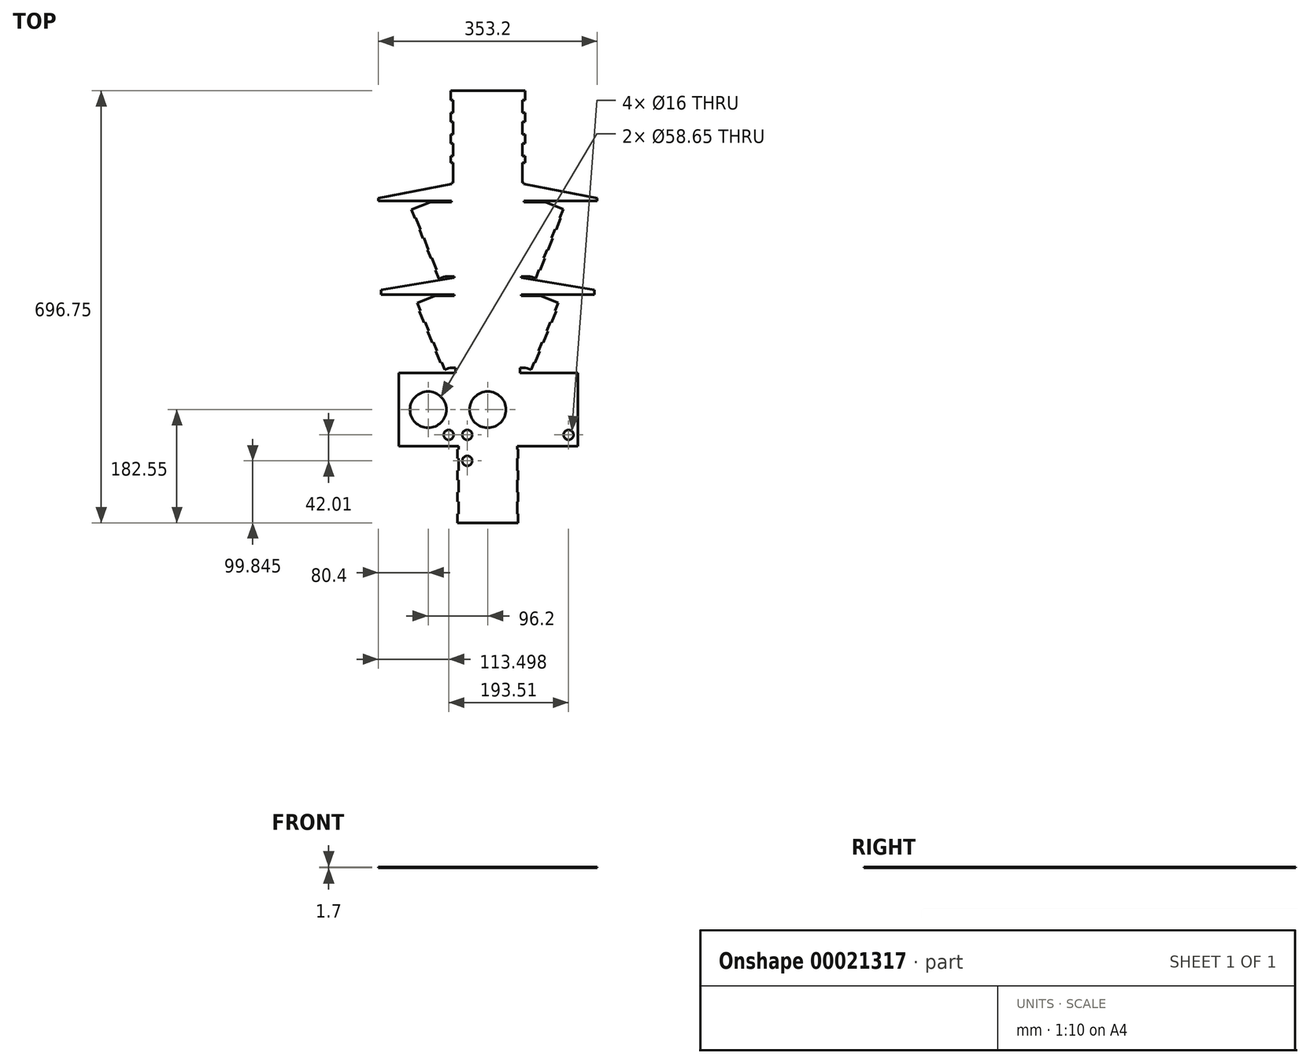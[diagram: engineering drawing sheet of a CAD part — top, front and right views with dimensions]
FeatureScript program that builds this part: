
annotation { "Feature Type Name" : "Feature", "Feature Type Description" : "" }
export const myFeature = defineFeature(function(context is Context, id is Id, definition is map)
    precondition{}
    {
        {
            var Q0;
            Q0=qCreatedBy(makeId("Top.planeOp"),FACE);
            var sketch = newSketch(context, id + "F0", { "sketchPlane" : qUnion([Q0])});
            skCircle(sketch, "E0", {"center": v(0, 0) * mm, "radius": 29.32 * mm, "construction": true});
            skCircle(sketch, "E1", {"center": v(0, 0) * mm, "radius": 34 * mm, "construction": true});
            skLineSegment(sketch, "E2.rect.bottom", {"start": v(60, 60) * mm, "end": v(-60, 60) * mm});
            skLineSegment(sketch, "E2.rect.top", {"start": v(60, -60) * mm, "end": v(-60, -60) * mm});
            skLineSegment(sketch, "E2.rect.left", {"start": v(60, 60) * mm, "end": v(60, -60) * mm});
            skLineSegment(sketch, "E2.rect.right", {"start": v(-60, 60) * mm, "end": v(-60, -60) * mm});
            skLineSegment(sketch, "E3", {"start": v(0, 42.22) * mm, "end": v(0, 43.92) * mm, "construction": true});
            skLineSegment(sketch, "E4", {"start": v(-60, 60) * mm, "end": v(-60, 91) * mm, "construction": true});
            skLineSegment(sketch, "E5", {"start": v(60, -60) * mm, "end": v(68, -60) * mm});
            skLineSegment(sketch, "E6", {"start": v(68, -60) * mm, "end": v(91, 60) * mm});
            skLineSegment(sketch, "E7", {"start": v(91, 60) * mm, "end": v(60, 60) * mm});
            skLineSegment(sketch, "E8", {"start": v(91, 60) * mm, "end": v(92.67, 59.68) * mm});
            skLineSegment(sketch, "E9", {"start": v(69.67, -60.32) * mm, "end": v(68, -60) * mm});
            skLineSegment(sketch, "E10", {"start": v(92.67, 59.68) * mm, "end": v(94.34, 59.36) * mm});
            skLineSegment(sketch, "E11", {"start": v(94.34, 59.36) * mm, "end": v(71.34, -60.64) * mm});
            skLineSegment(sketch, "E12", {"start": v(71.34, -60.64) * mm, "end": v(69.67, -60.32) * mm});
            skLineSegment(sketch, "E13", {"start": v(94.34, 59.36) * mm, "end": v(123.14, 47.9) * mm, "construction": true});
            skLineSegment(sketch, "E14", {"start": v(123.14, 47.9) * mm, "end": v(78.77, -63.6) * mm, "construction": true});
            skLineSegment(sketch, "E15", {"start": v(78.77, -63.6) * mm, "end": v(71.34, -60.64) * mm, "construction": true});
            skLineSegment(sketch, "E16", {"start": v(123.14, 47.9) * mm, "end": v(121.56, 48.53) * mm, "construction": true});
            skLineSegment(sketch, "E17", {"start": v(121.56, 48.53) * mm, "end": v(77.2, -62.97) * mm, "construction": true});
            skLineSegment(sketch, "E18", {"start": v(77.2, -62.97) * mm, "end": v(78.77, -63.6) * mm, "construction": true});
            skLineSegment(sketch, "E19", {"start": v(58.3, 89.3) * mm, "end": v(176.6, 66.3) * mm});
            skLineSegment(sketch, "E20.MirrorCS", {"start": v(-91, 60) * mm, "end": v(-60, 60) * mm});
            skLineSegment(sketch, "E21.MirrorCS", {"start": v(-68, -60) * mm, "end": v(-91, 60) * mm});
            skLineSegment(sketch, "E22.MirrorCS", {"start": v(-94.34, 59.36) * mm, "end": v(-123.14, 47.9) * mm});
            skLineSegment(sketch, "E23.MirrorCS", {"start": v(-94.34, 59.36) * mm, "end": v(-71.34, -60.64) * mm});
            skLineSegment(sketch, "E24.MirrorCS", {"start": v(-121.56, 48.53) * mm, "end": v(-77.2, -62.97) * mm, "construction": true});
            skLineSegment(sketch, "E25.MirrorCS", {"start": v(-123.14, 47.9) * mm, "end": v(-78.77, -63.6) * mm, "construction": true});
            skLineSegment(sketch, "E26.MirrorCS", {"start": v(-91, 60) * mm, "end": v(-92.67, 59.68) * mm});
            skLineSegment(sketch, "E27.MirrorCS", {"start": v(-92.67, 59.68) * mm, "end": v(-94.34, 59.36) * mm});
            skLineSegment(sketch, "E28.MirrorCS", {"start": v(-60, -60) * mm, "end": v(-68, -60) * mm});
            skLineSegment(sketch, "E29.MirrorCS", {"start": v(-69.67, -60.32) * mm, "end": v(-68, -60) * mm});
            skLineSegment(sketch, "E30.MirrorCS", {"start": v(-71.34, -60.64) * mm, "end": v(-69.67, -60.32) * mm});
            skLineSegment(sketch, "E31.MirrorCS", {"start": v(-78.77, -63.6) * mm, "end": v(-71.34, -60.64) * mm, "construction": true});
            skLineSegment(sketch, "E32", {"start": v(123.14, 47.9) * mm, "end": v(117.6, 33.96) * mm, "construction": true});
            skLineSegment(sketch, "E33", {"start": v(117.6, 33.96) * mm, "end": v(116.02, 34.59) * mm});
            skLineSegment(sketch, "E34", {"start": v(116.02, 34.59) * mm, "end": v(108.62, 16) * mm, "construction": true});
            skLineSegment(sketch, "E35", {"start": v(108.62, 16) * mm, "end": v(110.2, 15.38) * mm});
            skLineSegment(sketch, "E36", {"start": v(110.2, 15.38) * mm, "end": v(104.65, 1.44) * mm, "construction": true});
            skLineSegment(sketch, "E37", {"start": v(104.65, 1.44) * mm, "end": v(103.08, 2.07) * mm});
            skLineSegment(sketch, "E38", {"start": v(103.08, 2.07) * mm, "end": v(95.68, -16.51) * mm, "construction": true});
            skLineSegment(sketch, "E39", {"start": v(95.68, -16.51) * mm, "end": v(97.26, -17.14) * mm});
            skLineSegment(sketch, "E40", {"start": v(97.26, -17.14) * mm, "end": v(91.71, -31.08) * mm, "construction": true});
            skLineSegment(sketch, "E41", {"start": v(91.71, -31.08) * mm, "end": v(90.13, -30.45) * mm});
            skLineSegment(sketch, "E42", {"start": v(90.13, -30.45) * mm, "end": v(82.74, -49.03) * mm, "construction": true});
            skLineSegment(sketch, "E43", {"start": v(82.74, -49.03) * mm, "end": v(84.32, -49.66) * mm});
            skLineSegment(sketch, "E44", {"start": v(84.32, -49.66) * mm, "end": v(78.77, -63.6) * mm, "construction": true});
            skLineSegment(sketch, "E45", {"start": v(55.75, 122) * mm, "end": v(55.75, 91) * mm});
            skLineSegment(sketch, "E46", {"start": v(60, 91) * mm, "end": v(-60, 91) * mm, "construction": true});
            skLineSegment(sketch, "E47", {"start": v(-55.75, 92.7) * mm, "end": v(55.75, 92.7) * mm});
            skLineSegment(sketch, "E48", {"start": v(55.75, 122) * mm, "end": v(-55.75, 122) * mm});
            skLineSegment(sketch, "E49", {"start": v(55.75, 122) * mm, "end": v(55.75, 120.3) * mm, "construction": true});
            skLineSegment(sketch, "E50", {"start": v(-55.75, 239.45) * mm, "end": v(-55.75, 122) * mm, "construction": true});
            skLineSegment(sketch, "E51", {"start": v(55.75, 239.45) * mm, "end": v(-55.75, 239.45) * mm});
            skLineSegment(sketch, "E52", {"start": v(55.75, 120.3) * mm, "end": v(55.75, 118.6) * mm, "construction": true});
            skLineSegment(sketch, "E53", {"start": v(55.75, 119.45) * mm, "end": v(55.75, 239.45) * mm, "construction": true});
            skLineSegment(sketch, "E54", {"start": v(56.6, 91) * mm, "end": v(58.3, 91) * mm, "construction": true});
            skLineSegment(sketch, "E55", {"start": v(58.3, 91) * mm, "end": v(60, 91) * mm, "construction": true});
            skLineSegment(sketch, "E56", {"start": v(58.3, 61.7) * mm, "end": v(58.3, 60) * mm});
            skLineSegment(sketch, "E57", {"start": v(58.3, 89.3) * mm, "end": v(58.3, 91) * mm});
            skLineSegment(sketch, "E58", {"start": v(58.3, 89.3) * mm, "end": v(58.3, 61.7) * mm});
            skLineSegment(sketch, "E59", {"start": v(60, 91) * mm, "end": v(60, 60) * mm, "construction": true});
            skLineSegment(sketch, "E60", {"start": v(178.3, 60) * mm, "end": v(178.3, 68) * mm, "construction": true});
            skLineSegment(sketch, "E61", {"start": v(178.3, 61.7) * mm, "end": v(58.3, 61.7) * mm, "construction": true});
            skLineSegment(sketch, "E62", {"start": v(176.6, 66.3) * mm, "end": v(176.6, 61.7) * mm});
            skLineSegment(sketch, "E63", {"start": v(176.6, 61.7) * mm, "end": v(178.3, 61.7) * mm, "construction": true});
            skLineSegment(sketch, "E64", {"start": v(178.3, 61.7) * mm, "end": v(178.3, 60) * mm, "construction": true});
            skLineSegment(sketch, "E65", {"start": v(178.3, 68) * mm, "end": v(178.3, 66.3) * mm, "construction": true});
            skLineSegment(sketch, "E66.MirrorCS", {"start": v(-58.3, 89.3) * mm, "end": v(-176.6, 66.3) * mm});
            skLineSegment(sketch, "E67.MirrorCS", {"start": v(-176.6, 66.3) * mm, "end": v(-176.6, 61.7) * mm});
            skLineSegment(sketch, "E68.MirrorCS", {"start": v(-58.3, 89.3) * mm, "end": v(-58.3, 91) * mm});
            skLineSegment(sketch, "E69.MirrorCS", {"start": v(-58.3, 89.3) * mm, "end": v(-58.3, 61.7) * mm});
            skLineSegment(sketch, "E70.MirrorCS", {"start": v(-58.3, 61.7) * mm, "end": v(-58.3, 60) * mm});
            skLineSegment(sketch, "E71", {"start": v(176.6, 61.7) * mm, "end": v(58.3, 61.7) * mm});
            skLineSegment(sketch, "E72.MirrorCS", {"start": v(-176.6, 61.7) * mm, "end": v(-58.3, 61.7) * mm});
            skLineSegment(sketch, "E73", {"start": v(55.75, 92.7) * mm, "end": v(55.75, 91) * mm, "construction": true});
            skLineSegment(sketch, "E74", {"start": v(55.75, 239.45) * mm, "end": v(60, 239.45) * mm});
            skLineSegment(sketch, "E75", {"start": v(60, 239.45) * mm, "end": v(60, 224.45) * mm});
            skLineSegment(sketch, "E76", {"start": v(60, 224.45) * mm, "end": v(55.75, 224.45) * mm});
            skLineSegment(sketch, "E77", {"start": v(55.75, 224.45) * mm, "end": v(55.75, 204.45) * mm});
            skLineSegment(sketch, "E78", {"start": v(55.75, 204.45) * mm, "end": v(60, 204.45) * mm});
            skLineSegment(sketch, "E79", {"start": v(60, 204.45) * mm, "end": v(60, 189.45) * mm});
            skLineSegment(sketch, "E80", {"start": v(60, 189.45) * mm, "end": v(55.75, 189.45) * mm});
            skLineSegment(sketch, "E81", {"start": v(55.75, 189.45) * mm, "end": v(55.75, 169.45) * mm});
            skLineSegment(sketch, "E82", {"start": v(55.75, 169.45) * mm, "end": v(60, 169.45) * mm});
            skLineSegment(sketch, "E83", {"start": v(60, 169.45) * mm, "end": v(60, 154.45) * mm});
            skLineSegment(sketch, "E84", {"start": v(60, 154.45) * mm, "end": v(55.75, 154.45) * mm});
            skLineSegment(sketch, "E85", {"start": v(55.75, 154.45) * mm, "end": v(55.75, 134.45) * mm});
            skLineSegment(sketch, "E86", {"start": v(55.75, 134.45) * mm, "end": v(60, 134.45) * mm});
            skLineSegment(sketch, "E87", {"start": v(60, 134.45) * mm, "end": v(60, 123.7) * mm});
            skLineSegment(sketch, "E88", {"start": v(55.75, 123.7) * mm, "end": v(55.75, 122) * mm, "construction": true});
            skLineSegment(sketch, "E89", {"start": v(55.75, 123.7) * mm, "end": v(55.75, 122) * mm});
            skLineSegment(sketch, "E90", {"start": v(60, 123.7) * mm, "end": v(55.75, 123.7) * mm});
            skLineSegment(sketch, "E91", {"start": v(55.75, -91) * mm, "end": v(-55.75, -91) * mm});
            skLineSegment(sketch, "E92", {"start": v(-55.75, -91) * mm, "end": v(-55.75, -60) * mm, "construction": true});
            skLineSegment(sketch, "E93", {"start": v(55.75, -91) * mm, "end": v(55.75, -60) * mm, "construction": true});
            skLineSegment(sketch, "E94", {"start": v(55.75, -60) * mm, "end": v(54.05, -60) * mm});
            skLineSegment(sketch, "E95", {"start": v(54.05, -60) * mm, "end": v(54.05, -61.7) * mm});
            skLineSegment(sketch, "E96", {"start": v(54.05, -61.7) * mm, "end": v(172.35, -81.3) * mm});
            skLineSegment(sketch, "E97", {"start": v(54.05, -91) * mm, "end": v(54.05, -89.3) * mm});
            skLineSegment(sketch, "E98", {"start": v(54.05, -89.3) * mm, "end": v(172.35, -89.3) * mm});
            skLineSegment(sketch, "E99", {"start": v(172.35, -89.3) * mm, "end": v(172.35, -81.3) * mm});
            skLineSegment(sketch, "E100", {"start": v(57.45, 91) * mm, "end": v(55.75, 91) * mm});
            skLineSegment(sketch, "E101", {"start": v(-60, -60) * mm, "end": v(-55.75, -60) * mm});
            skLineSegment(sketch, "E102", {"start": v(55.75, -60) * mm, "end": v(60, -60) * mm});
            skLineSegment(sketch, "E103.MirrorCS", {"start": v(-172.35, -89.3) * mm, "end": v(-172.35, -81.3) * mm});
            skLineSegment(sketch, "E104.MirrorCS", {"start": v(-54.05, -61.7) * mm, "end": v(-172.35, -81.3) * mm});
            skLineSegment(sketch, "E105.MirrorCS", {"start": v(-54.05, -89.3) * mm, "end": v(-172.35, -89.3) * mm});
            skLineSegment(sketch, "E106.MirrorCS", {"start": v(-54.05, -60) * mm, "end": v(-54.05, -61.7) * mm});
            skLineSegment(sketch, "E107.MirrorCS", {"start": v(-55.75, -60) * mm, "end": v(-54.05, -60) * mm});
            skLineSegment(sketch, "E108.MirrorCS", {"start": v(-54.05, -91) * mm, "end": v(-54.05, -89.3) * mm, "construction": true});
            skLineSegment(sketch, "E109", {"start": v(54.05, -91) * mm, "end": v(52.35, -91) * mm, "construction": true});
            skLineSegment(sketch, "E110", {"start": v(-54.05, -91) * mm, "end": v(-52.35, -91) * mm, "construction": true});
            skLineSegment(sketch, "E111", {"start": v(52.35, -91) * mm, "end": v(52.35, -211) * mm});
            skLineSegment(sketch, "E112", {"start": v(52.35, -211) * mm, "end": v(52.35, -209.3) * mm, "construction": true});
            skLineSegment(sketch, "E113", {"start": v(52.35, -209.3) * mm, "end": v(52.35, -207.6) * mm, "construction": true});
            skLineSegment(sketch, "E114", {"start": v(52.35, -207.6) * mm, "end": v(-52.35, -207.6) * mm});
            skLineSegment(sketch, "E115", {"start": v(-52.35, -207.6) * mm, "end": v(-52.35, -91) * mm});
            skLineSegment(sketch, "E116", {"start": v(52.35, -207.6) * mm, "end": v(60.35, -207.6) * mm});
            skLineSegment(sketch, "E117", {"start": v(60.35, -207.6) * mm, "end": v(83.35, -91) * mm});
            skLineSegment(sketch, "E118", {"start": v(83.35, -91) * mm, "end": v(52.35, -91) * mm, "construction": true});
            skLineSegment(sketch, "E119", {"start": v(83.35, -91) * mm, "end": v(86.69, -91.66) * mm});
            skLineSegment(sketch, "E120", {"start": v(86.69, -91.66) * mm, "end": v(63.69, -208.26) * mm});
            skLineSegment(sketch, "E121", {"start": v(60.35, -207.6) * mm, "end": v(62.02, -207.93) * mm});
            skLineSegment(sketch, "E122", {"start": v(62.02, -207.93) * mm, "end": v(63.69, -208.26) * mm});
            skLineSegment(sketch, "E123", {"start": v(86.69, -91.66) * mm, "end": v(115.36, -103.43) * mm, "construction": true});
            skLineSegment(sketch, "E124", {"start": v(115.36, -103.43) * mm, "end": v(71.09, -211.3) * mm, "construction": true});
            skLineSegment(sketch, "E125", {"start": v(71.09, -211.3) * mm, "end": v(63.69, -208.26) * mm, "construction": true});
            skLineSegment(sketch, "E126", {"start": v(-52.35, -207.6) * mm, "end": v(-60.35, -207.6) * mm});
            skLineSegment(sketch, "E127", {"start": v(-60.35, -207.6) * mm, "end": v(-83.35, -91) * mm});
            skLineSegment(sketch, "E128", {"start": v(-83.35, -91) * mm, "end": v(-52.35, -91) * mm, "construction": true});
            skLineSegment(sketch, "E129", {"start": v(-83.35, -91) * mm, "end": v(-86.69, -91.66) * mm});
            skLineSegment(sketch, "E130", {"start": v(-86.69, -91.66) * mm, "end": v(-63.69, -208.26) * mm});
            skLineSegment(sketch, "E131", {"start": v(-63.69, -208.26) * mm, "end": v(-60.35, -207.6) * mm});
            skLineSegment(sketch, "E132", {"start": v(-86.69, -91.66) * mm, "end": v(-115.36, -103.43) * mm, "construction": true});
            skLineSegment(sketch, "E133", {"start": v(-115.36, -103.43) * mm, "end": v(-71.09, -211.3) * mm, "construction": true});
            skLineSegment(sketch, "E134", {"start": v(-71.09, -211.3) * mm, "end": v(-63.69, -208.26) * mm, "construction": true});
            skLineSegment(sketch, "E135", {"start": v(-47.25, -215.6) * mm, "end": v(47.25, -215.6) * mm});
            skLineSegment(sketch, "E136", {"start": v(47.25, -215.6) * mm, "end": v(47.25, -332.2) * mm});
            skLineSegment(sketch, "E137", {"start": v(-47.25, -333.9) * mm, "end": v(-47.25, -215.6) * mm});
            skLineSegment(sketch, "E138", {"start": v(47.25, -333.9) * mm, "end": v(47.25, -332.2) * mm, "construction": true});
            skLineSegment(sketch, "E139", {"start": v(47.25, -333.9) * mm, "end": v(-47.25, -333.9) * mm});
            skLineSegment(sketch, "E140", {"start": v(50.65, -215.6) * mm, "end": v(50.65, -333.9) * mm});
            skLineSegment(sketch, "E141", {"start": v(50.65, -333.9) * mm, "end": v(47.25, -333.9) * mm});
            skLineSegment(sketch, "E142", {"start": v(47.25, -215.6) * mm, "end": v(48.95, -215.6) * mm, "construction": true});
            skLineSegment(sketch, "E143", {"start": v(48.95, -215.6) * mm, "end": v(50.65, -215.6) * mm, "construction": true});
            skLineSegment(sketch, "E144", {"start": v(-47.25, -215.6) * mm, "end": v(-48.95, -215.6) * mm, "construction": true});
            skLineSegment(sketch, "E145", {"start": v(-48.95, -215.6) * mm, "end": v(-48.95, -333.9) * mm});
            skLineSegment(sketch, "E146", {"start": v(-48.95, -333.9) * mm, "end": v(-47.25, -333.9) * mm});
            skLineSegment(sketch, "E147", {"start": v(0, -215.6) * mm, "end": v(0, -274.75) * mm, "construction": true});
            skLineSegment(sketch, "E148", {"start": v(0, -274.75) * mm, "end": v(-47.25, -274.75) * mm, "construction": true});
            skCircle(sketch, "E149", {"center": v(0, -274.75) * mm, "radius": 29.32 * mm});
            skLineSegment(sketch, "E150", {"start": v(52.35, -207.6) * mm, "end": v(50.65, -207.6) * mm, "construction": true});
            skLineSegment(sketch, "E151", {"start": v(50.65, -207.6) * mm, "end": v(48.95, -207.6) * mm, "construction": true});
            skLineSegment(sketch, "E152", {"start": v(48.95, -207.6) * mm, "end": v(47.25, -207.6) * mm, "construction": true});
            skLineSegment(sketch, "E153", {"start": v(47.25, -215.6) * mm, "end": v(-47.25, -215.6) * mm});
            skPoint(sketch, "E154", {"position": v(0, -207.6) * mm});
            skPoint(sketch, "E155", {"position": v(0, -215.6) * mm});
            skLineSegment(sketch, "E156", {"start": v(-47.25, -207.6) * mm, "end": v(-52.35, -207.6) * mm, "construction": true});
            skLineSegment(sketch, "E157", {"start": v(-52.35, -207.6) * mm, "end": v(-52.35, -215.6) * mm});
            skLineSegment(sketch, "E158", {"start": v(-52.35, -215.6) * mm, "end": v(-47.25, -215.6) * mm, "construction": true});
            skLineSegment(sketch, "E159", {"start": v(52.35, -207.6) * mm, "end": v(52.35, -215.6) * mm});
            skLineSegment(sketch, "E160", {"start": v(52.35, -215.6) * mm, "end": v(47.25, -215.6) * mm, "construction": true});
            skLineSegment(sketch, "E161", {"start": v(-48.95, -333.9) * mm, "end": v(-143.45, -333.9) * mm});
            skLineSegment(sketch, "E162", {"start": v(-143.45, -333.9) * mm, "end": v(-143.45, -215.6) * mm});
            skLineSegment(sketch, "E163", {"start": v(-143.45, -215.6) * mm, "end": v(-48.95, -215.6) * mm, "construction": true});
            skLineSegment(sketch, "E164", {"start": v(50.65, -215.6) * mm, "end": v(145.15, -215.6) * mm, "construction": true});
            skLineSegment(sketch, "E165", {"start": v(145.15, -215.6) * mm, "end": v(145.15, -333.9) * mm});
            skLineSegment(sketch, "E166", {"start": v(145.15, -333.9) * mm, "end": v(50.65, -333.9) * mm});
            skLineSegment(sketch, "E167", {"start": v(-47.25, -333.9) * mm, "end": v(-47.25, -339) * mm});
            skLineSegment(sketch, "E168", {"start": v(-47.25, -339) * mm, "end": v(47.25, -339) * mm});
            skLineSegment(sketch, "E169", {"start": v(47.25, -333.9) * mm, "end": v(47.25, -335.6) * mm});
            skLineSegment(sketch, "E170", {"start": v(47.25, -335.6) * mm, "end": v(47.25, -339) * mm});
            skLineSegment(sketch, "E171", {"start": v(-47.25, -339) * mm, "end": v(-47.25, -457.3) * mm, "construction": true});
            skLineSegment(sketch, "E172", {"start": v(-47.25, -457.3) * mm, "end": v(47.25, -457.3) * mm});
            skLineSegment(sketch, "E173", {"start": v(47.25, -457.3) * mm, "end": v(47.25, -339) * mm, "construction": true});
            skLineSegment(sketch, "E174", {"start": v(-96.2, -215.6) * mm, "end": v(-96.2, -274.75) * mm, "construction": true});
            skLineSegment(sketch, "E175", {"start": v(-96.2, -274.75) * mm, "end": v(-48.95, -274.75) * mm, "construction": true});
            skCircle(sketch, "E176", {"center": v(-96.2, -274.75) * mm, "radius": 29.32 * mm});
            skLineSegment(sketch, "E177", {"start": v(47.25, -457.3) * mm, "end": v(48.95, -457.3) * mm});
            skLineSegment(sketch, "E178", {"start": v(48.95, -339) * mm, "end": v(47.25, -339) * mm});
            skLineSegment(sketch, "E179", {"start": v(-47.25, -339) * mm, "end": v(-48.95, -339) * mm});
            skLineSegment(sketch, "E180", {"start": v(-48.95, -457.3) * mm, "end": v(-47.25, -457.3) * mm});
            skLineSegment(sketch, "E181", {"start": v(48.95, -339) * mm, "end": v(48.95, -353.15) * mm});
            skLineSegment(sketch, "E182", {"start": v(48.95, -353.15) * mm, "end": v(47.25, -353.15) * mm});
            skLineSegment(sketch, "E183", {"start": v(47.25, -353.15) * mm, "end": v(47.25, -373.15) * mm});
            skLineSegment(sketch, "E184", {"start": v(47.25, -373.15) * mm, "end": v(48.95, -373.15) * mm});
            skLineSegment(sketch, "E185", {"start": v(48.95, -373.15) * mm, "end": v(48.95, -388.15) * mm});
            skLineSegment(sketch, "E186", {"start": v(48.95, -388.15) * mm, "end": v(47.25, -388.15) * mm});
            skLineSegment(sketch, "E187", {"start": v(47.25, -408.15) * mm, "end": v(47.25, -388.15) * mm});
            skLineSegment(sketch, "E188", {"start": v(47.25, -408.15) * mm, "end": v(48.95, -408.15) * mm});
            skLineSegment(sketch, "E189", {"start": v(48.95, -408.15) * mm, "end": v(48.95, -423.15) * mm});
            skLineSegment(sketch, "E190", {"start": v(48.95, -423.15) * mm, "end": v(47.25, -423.15) * mm});
            skLineSegment(sketch, "E191", {"start": v(47.25, -423.15) * mm, "end": v(47.25, -443.15) * mm});
            skLineSegment(sketch, "E192", {"start": v(47.25, -443.15) * mm, "end": v(48.95, -443.15) * mm});
            skLineSegment(sketch, "E193", {"start": v(48.95, -443.15) * mm, "end": v(48.95, -457.3) * mm});
            skLineSegment(sketch, "E194.MirrorCS", {"start": v(-48.95, -443.15) * mm, "end": v(-48.95, -457.3) * mm});
            skLineSegment(sketch, "E195.MirrorCS", {"start": v(-48.95, -408.15) * mm, "end": v(-48.95, -423.15) * mm});
            skLineSegment(sketch, "E196.MirrorCS", {"start": v(-48.95, -373.15) * mm, "end": v(-48.95, -388.15) * mm});
            skLineSegment(sketch, "E197.MirrorCS", {"start": v(-48.95, -339) * mm, "end": v(-48.95, -353.15) * mm});
            skLineSegment(sketch, "E198.MirrorCS", {"start": v(-48.95, -339) * mm, "end": v(-47.25, -339) * mm});
            skLineSegment(sketch, "E199.MirrorCS", {"start": v(-48.95, -353.15) * mm, "end": v(-47.25, -353.15) * mm});
            skLineSegment(sketch, "E200.MirrorCS", {"start": v(-47.25, -373.15) * mm, "end": v(-48.95, -373.15) * mm});
            skLineSegment(sketch, "E201.MirrorCS", {"start": v(-48.95, -388.15) * mm, "end": v(-47.25, -388.15) * mm});
            skLineSegment(sketch, "E202.MirrorCS", {"start": v(-47.25, -408.15) * mm, "end": v(-48.95, -408.15) * mm});
            skLineSegment(sketch, "E203.MirrorCS", {"start": v(-48.95, -423.15) * mm, "end": v(-47.25, -423.15) * mm});
            skLineSegment(sketch, "E204.MirrorCS", {"start": v(-47.25, -457.3) * mm, "end": v(-48.95, -457.3) * mm});
            skLineSegment(sketch, "E205.MirrorCS", {"start": v(-47.25, -443.15) * mm, "end": v(-48.95, -443.15) * mm});
            skLineSegment(sketch, "E206.MirrorCS", {"start": v(-47.25, -423.15) * mm, "end": v(-47.25, -443.15) * mm});
            skLineSegment(sketch, "E207.MirrorCS", {"start": v(-47.25, -353.15) * mm, "end": v(-47.25, -373.15) * mm});
            skLineSegment(sketch, "E208.MirrorCS", {"start": v(-47.25, -408.15) * mm, "end": v(-47.25, -388.15) * mm});
            skLineSegment(sketch, "E209.MirrorCS", {"start": v(-82.74, -49.03) * mm, "end": v(-84.32, -49.66) * mm});
            skLineSegment(sketch, "E210.MirrorCS", {"start": v(-77.2, -62.97) * mm, "end": v(-78.77, -63.6) * mm});
            skLineSegment(sketch, "E211.MirrorCS", {"start": v(-84.32, -49.66) * mm, "end": v(-78.77, -63.6) * mm});
            skLineSegment(sketch, "E212.MirrorCS", {"start": v(-90.13, -30.45) * mm, "end": v(-82.74, -49.03) * mm});
            skLineSegment(sketch, "E213.MirrorCS", {"start": v(-91.71, -31.08) * mm, "end": v(-90.13, -30.45) * mm});
            skLineSegment(sketch, "E214.MirrorCS", {"start": v(-97.26, -17.14) * mm, "end": v(-91.71, -31.08) * mm});
            skLineSegment(sketch, "E215.MirrorCS", {"start": v(-95.68, -16.51) * mm, "end": v(-97.26, -17.14) * mm});
            skLineSegment(sketch, "E216.MirrorCS", {"start": v(-104.65, 1.44) * mm, "end": v(-103.08, 2.07) * mm});
            skLineSegment(sketch, "E217.MirrorCS", {"start": v(-103.08, 2.07) * mm, "end": v(-95.68, -16.51) * mm});
            skLineSegment(sketch, "E218.MirrorCS", {"start": v(-108.62, 16) * mm, "end": v(-110.2, 15.38) * mm});
            skLineSegment(sketch, "E219.MirrorCS", {"start": v(-110.2, 15.38) * mm, "end": v(-104.65, 1.44) * mm});
            skLineSegment(sketch, "E220.MirrorCS", {"start": v(-117.6, 33.96) * mm, "end": v(-116.02, 34.59) * mm});
            skLineSegment(sketch, "E221.MirrorCS", {"start": v(-116.02, 34.59) * mm, "end": v(-108.62, 16) * mm});
            skLineSegment(sketch, "E222.MirrorCS", {"start": v(-123.14, 47.9) * mm, "end": v(-121.56, 48.53) * mm});
            skLineSegment(sketch, "E223.MirrorCS", {"start": v(-123.14, 47.9) * mm, "end": v(-117.6, 33.96) * mm});
            skLineSegment(sketch, "E224.MirrorCS", {"start": v(-60, 204.45) * mm, "end": v(-60, 189.45) * mm});
            skLineSegment(sketch, "E225.MirrorCS", {"start": v(-60, 189.45) * mm, "end": v(-55.75, 189.45) * mm});
            skLineSegment(sketch, "E226.MirrorCS", {"start": v(-55.75, 189.45) * mm, "end": v(-55.75, 169.45) * mm});
            skLineSegment(sketch, "E227.MirrorCS", {"start": v(-55.75, 204.45) * mm, "end": v(-60, 204.45) * mm});
            skLineSegment(sketch, "E228.MirrorCS", {"start": v(-55.75, 169.45) * mm, "end": v(-60, 169.45) * mm});
            skLineSegment(sketch, "E229.MirrorCS", {"start": v(-60, 169.45) * mm, "end": v(-60, 154.45) * mm});
            skLineSegment(sketch, "E230.MirrorCS", {"start": v(-60, 154.45) * mm, "end": v(-55.75, 154.45) * mm});
            skLineSegment(sketch, "E231.MirrorCS", {"start": v(-55.75, 154.45) * mm, "end": v(-55.75, 134.45) * mm});
            skLineSegment(sketch, "E232.MirrorCS", {"start": v(-55.75, 134.45) * mm, "end": v(-60, 134.45) * mm});
            skLineSegment(sketch, "E233.MirrorCS", {"start": v(-55.75, 224.45) * mm, "end": v(-55.75, 204.45) * mm});
            skLineSegment(sketch, "E234.MirrorCS", {"start": v(-55.75, 239.45) * mm, "end": v(-60, 239.45) * mm});
            skLineSegment(sketch, "E235.MirrorCS", {"start": v(-60, 239.45) * mm, "end": v(-60, 224.45) * mm});
            skLineSegment(sketch, "E236.MirrorCS", {"start": v(-60, 224.45) * mm, "end": v(-55.75, 224.45) * mm});
            skLineSegment(sketch, "E237.MirrorCS", {"start": v(-60, 134.45) * mm, "end": v(-60, 123.7) * mm});
            skLineSegment(sketch, "E238.MirrorCS", {"start": v(-60, 123.7) * mm, "end": v(-55.75, 123.7) * mm});
            skPoint(sketch, "E239", {"position": v(0, 92.7) * mm});
            skPoint(sketch, "E240", {"position": v(0, 60) * mm});
            skLineSegment(sketch, "E241", {"start": v(-55.75, 92.7) * mm, "end": v(-55.75, 91) * mm});
            skLineSegment(sketch, "E242", {"start": v(-55.75, 122) * mm, "end": v(-55.75, 92.7) * mm});
            skLineSegment(sketch, "E243", {"start": v(-55.75, 123.7) * mm, "end": v(-55.75, 122) * mm});
            skLineSegment(sketch, "E244", {"start": v(-58.3, 91) * mm, "end": v(-55.75, 91) * mm});
            skLineSegment(sketch, "E245", {"start": v(-58.3, 60) * mm, "end": v(-60, 60) * mm});
            skLineSegment(sketch, "E246", {"start": v(-77.2, -62.97) * mm, "end": v(-71.34, -60.64) * mm});
            skLineSegment(sketch, "E247", {"start": v(-52.35, -91) * mm, "end": v(-54.05, -91) * mm, "construction": true});
            skLineSegment(sketch, "E248", {"start": v(-55.75, -91) * mm, "end": v(-83.35, -91) * mm});
            skLineSegment(sketch, "E249", {"start": v(58.3, 60) * mm, "end": v(60, 60) * mm});
            skLineSegment(sketch, "E250", {"start": v(94.34, 59.36) * mm, "end": v(121.56, 48.53) * mm});
            skLineSegment(sketch, "E251", {"start": v(121.56, 48.53) * mm, "end": v(116.02, 34.59) * mm});
            skLineSegment(sketch, "E252", {"start": v(117.6, 33.96) * mm, "end": v(110.2, 15.38) * mm});
            skLineSegment(sketch, "E253", {"start": v(108.62, 16) * mm, "end": v(103.08, 2.07) * mm});
            skLineSegment(sketch, "E254", {"start": v(104.65, 1.44) * mm, "end": v(97.26, -17.14) * mm});
            skLineSegment(sketch, "E255", {"start": v(95.68, -16.51) * mm, "end": v(90.13, -30.45) * mm});
            skLineSegment(sketch, "E256", {"start": v(91.71, -31.08) * mm, "end": v(84.32, -49.66) * mm});
            skLineSegment(sketch, "E257", {"start": v(82.74, -49.03) * mm, "end": v(77.2, -62.97) * mm});
            skLineSegment(sketch, "E258", {"start": v(77.2, -62.97) * mm, "end": v(71.34, -60.64) * mm});
            skLineSegment(sketch, "E259", {"start": v(-71.09, -211.3) * mm, "end": v(-69.51, -210.65) * mm, "construction": true});
            skLineSegment(sketch, "E260", {"start": v(-69.51, -210.65) * mm, "end": v(-74.56, -198.35) * mm});
            skLineSegment(sketch, "E261", {"start": v(-74.56, -198.35) * mm, "end": v(-76.14, -199) * mm});
            skLineSegment(sketch, "E262", {"start": v(-76.14, -199) * mm, "end": v(-83.73, -180.5) * mm});
            skLineSegment(sketch, "E263", {"start": v(-83.73, -180.5) * mm, "end": v(-82.16, -179.84) * mm});
            skLineSegment(sketch, "E264", {"start": v(-82.16, -179.84) * mm, "end": v(-87.86, -165.97) * mm});
            skLineSegment(sketch, "E265", {"start": v(-87.86, -165.97) * mm, "end": v(-89.43, -166.61) * mm});
            skLineSegment(sketch, "E266", {"start": v(-89.43, -166.61) * mm, "end": v(-97.02, -148.11) * mm});
            skLineSegment(sketch, "E267", {"start": v(-97.02, -148.11) * mm, "end": v(-95.45, -147.47) * mm});
            skLineSegment(sketch, "E268", {"start": v(-95.45, -147.47) * mm, "end": v(-101.15, -133.59) * mm});
            skLineSegment(sketch, "E269", {"start": v(-101.15, -133.59) * mm, "end": v(-102.72, -134.24) * mm});
            skLineSegment(sketch, "E270", {"start": v(-102.72, -134.24) * mm, "end": v(-110.31, -115.73) * mm});
            skLineSegment(sketch, "E271", {"start": v(-110.31, -115.73) * mm, "end": v(-108.74, -115.09) * mm});
            skLineSegment(sketch, "E272", {"start": v(-108.74, -115.09) * mm, "end": v(-113.8, -102.78) * mm});
            skLineSegment(sketch, "E273", {"start": v(-113.8, -102.78) * mm, "end": v(-115.36, -103.43) * mm, "construction": true});
            skLineSegment(sketch, "E274", {"start": v(-63.69, -208.26) * mm, "end": v(-69.51, -210.65) * mm});
            skLineSegment(sketch, "E275", {"start": v(-113.8, -102.78) * mm, "end": v(-86.69, -91.66) * mm});
            skLineSegment(sketch, "E276.MirrorCS", {"start": v(113.8, -102.78) * mm, "end": v(86.69, -91.66) * mm});
            skLineSegment(sketch, "E277.MirrorCS", {"start": v(108.74, -115.09) * mm, "end": v(113.8, -102.78) * mm});
            skLineSegment(sketch, "E278.MirrorCS", {"start": v(101.15, -133.59) * mm, "end": v(102.72, -134.24) * mm});
            skLineSegment(sketch, "E279.MirrorCS", {"start": v(110.31, -115.73) * mm, "end": v(108.74, -115.09) * mm});
            skLineSegment(sketch, "E280.MirrorCS", {"start": v(102.72, -134.24) * mm, "end": v(110.31, -115.73) * mm});
            skLineSegment(sketch, "E281.MirrorCS", {"start": v(82.16, -179.84) * mm, "end": v(87.86, -165.97) * mm});
            skLineSegment(sketch, "E282.MirrorCS", {"start": v(87.86, -165.97) * mm, "end": v(89.43, -166.61) * mm});
            skLineSegment(sketch, "E283.MirrorCS", {"start": v(89.43, -166.61) * mm, "end": v(97.02, -148.11) * mm});
            skLineSegment(sketch, "E284.MirrorCS", {"start": v(97.02, -148.11) * mm, "end": v(95.45, -147.47) * mm});
            skLineSegment(sketch, "E285.MirrorCS", {"start": v(95.45, -147.47) * mm, "end": v(101.15, -133.59) * mm});
            skLineSegment(sketch, "E286.MirrorCS", {"start": v(83.73, -180.5) * mm, "end": v(82.16, -179.84) * mm});
            skLineSegment(sketch, "E287.MirrorCS", {"start": v(76.14, -199) * mm, "end": v(83.73, -180.5) * mm});
            skLineSegment(sketch, "E288.MirrorCS", {"start": v(74.56, -198.35) * mm, "end": v(76.14, -199) * mm});
            skLineSegment(sketch, "E289.MirrorCS", {"start": v(69.51, -210.65) * mm, "end": v(74.56, -198.35) * mm});
            skLineSegment(sketch, "E290.MirrorCS", {"start": v(71.09, -211.3) * mm, "end": v(69.51, -210.65) * mm, "construction": true});
            skLineSegment(sketch, "E291.MirrorCS", {"start": v(63.69, -208.26) * mm, "end": v(69.51, -210.65) * mm});
            skLineSegment(sketch, "E292", {"start": v(54.05, -91) * mm, "end": v(83.35, -91) * mm});
            skLineSegment(sketch, "E293", {"start": v(-54.05, -89.3) * mm, "end": v(-54.05, -91) * mm});
            skLineSegment(sketch, "E294", {"start": v(-55.75, -91) * mm, "end": v(-54.05, -91) * mm});
            skLineSegment(sketch, "E295", {"start": v(-143.45, -215.6) * mm, "end": v(-52.35, -215.6) * mm});
            skLineSegment(sketch, "E296", {"start": v(145.15, -215.6) * mm, "end": v(52.35, -215.6) * mm});
            skLineSegment(sketch, "E297", {"start": v(57.45, 91) * mm, "end": v(58.3, 91) * mm});
            skLineSegment(sketch, "E298", {"start": v(-55.75, 91) * mm, "end": v(55.75, 91) * mm});
            skLineSegment(sketch, "E299", {"start": v(-96.2, -274.75) * mm, "end": v(-48.95, -333.9) * mm, "construction": true});
            skCircle(sketch, "E300", {"center": v(-63.1, -315.44) * mm, "radius": 18.46 * mm, "construction": true});
            skCircle(sketch, "E301", {"center": v(-63.1, -315.44) * mm, "radius": 8 * mm});
            skLineSegment(sketch, "E302", {"start": v(-48.1, -333.9) * mm, "end": v(-48.1, -274.75) * mm, "construction": true});
            skCircle(sketch, "E303.MirrorC", {"center": v(-33.1, -315.44) * mm, "radius": 8 * mm});
            skLineSegment(sketch, "E304", {"start": v(0, -274.75) * mm, "end": v(-33.1, -315.44) * mm, "construction": true});
            skLineSegment(sketch, "E305", {"start": v(50.65, -274.75) * mm, "end": v(97.9, -274.75) * mm, "construction": true});
            skCircle(sketch, "E306", {"center": v(97.9, -274.75) * mm, "radius": 29.32 * mm, "construction": true});
            skLineSegment(sketch, "E307", {"start": v(97.9, -274.75) * mm, "end": v(145.15, -333.9) * mm, "construction": true});
            skCircle(sketch, "E308", {"center": v(130.4, -315.44) * mm, "radius": 8 * mm});
            skLineSegment(sketch, "E309", {"start": v(-63.1, -315.44) * mm, "end": v(-33.1, -315.44) * mm, "construction": true});
            skLineSegment(sketch, "E310", {"start": v(-33.1, -315.44) * mm, "end": v(130.4, -315.44) * mm, "construction": true});
            skCircle(sketch, "E311", {"center": v(-96.2, -274.75) * mm, "radius": 34 * mm, "construction": true});
            skLineSegment(sketch, "E312", {"start": v(-47.25, -336.45) * mm, "end": v(-25.77, -336.45) * mm, "construction": true});
            skCircle(sketch, "E313.MirrorC", {"center": v(-33.1, -357.46) * mm, "radius": 8 * mm});
            skLineSegment(sketch, "E314", {"start": v(-48.95, -333.9) * mm, "end": v(-57.75, -325.1) * mm, "construction": true});
            skSolve(sketch);
        }
        {
            var Q0;
            Q0=makeQuery(id+"F0.imprint","IMPRINT",FACE,{"disambiguationData":[TD([[makeQuery(id+"F0.imprint","IMPRINT",EDGE,{"derivedFrom":sQuery(id+"F0.wireOp",EDGE,"E48")}),-1.0]])]});
            var Q1;
            {var subQ4=sQuery(id+"F0.wireOp",EDGE,"E111");Q1=makeQuery(id+"F0.imprint","IMPRINT",FACE,{"disambiguationData":[TD([[makeQuery(id+"F0.imprint","IMPRINT",EDGE,{"derivedFrom":subQ4}),1.0]])]});}
            var Q2;
            {var subQ1=sQuery(id+"F0.wireOp",EDGE,"E115");Q2=makeQuery(id+"F0.imprint","IMPRINT",FACE,{"disambiguationData":[TD([[makeQuery(id+"F0.imprint","IMPRINT",EDGE,{"derivedFrom":subQ1}),1.0]])]});}
            var Q3;
            Q3=makeQuery(id+"F0.imprint","IMPRINT",FACE,{"disambiguationData":[TD([[makeQuery(id+"F0.imprint","IMPRINT",EDGE,{"derivedFrom":sQuery(id+"F0.wireOp",EDGE,"E2.rect.bottom")}),1.0]])]});
            var Q4;
            Q4=makeQuery(id+"F0.imprint","IMPRINT",FACE,{"disambiguationData":[TD([[makeQuery(id+"F0.imprint","IMPRINT",EDGE,{"derivedFrom":sQuery(id+"F0.wireOp",EDGE,"E2.rect.bottom")}),-1.0]])]});
            var Q5;
            {var subQ1=sQuery(id+"F0.wireOp",EDGE,"E47");Q5=makeQuery(id+"F0.imprint","IMPRINT",FACE,{"disambiguationData":[TD([[makeQuery(id+"F0.imprint","IMPRINT",EDGE,{"derivedFrom":subQ1}),1.0]])]});}
            var Q6;
            Q6=makeQuery(id+"F0.imprint","IMPRINT",FACE,{"disambiguationData":[TD([[makeQuery(id+"F0.imprint","IMPRINT",EDGE,{"derivedFrom":sQuery(id+"F0.wireOp",EDGE,"E11")}),1.0]])]});
            var Q7;
            Q7=makeQuery(id+"F0.imprint","IMPRINT",FACE,{"disambiguationData":[TD([[makeQuery(id+"F0.imprint","IMPRINT",EDGE,{"derivedFrom":sQuery(id+"F0.wireOp",EDGE,"E19")}),-1.0]])]});
            var Q8;
            Q8=makeQuery(id+"F0.imprint","IMPRINT",FACE,{"disambiguationData":[TD([[makeQuery(id+"F0.imprint","IMPRINT",EDGE,{"derivedFrom":sQuery(id+"F0.wireOp",EDGE,"E22.MirrorCS")}),1.0]])]});
            var Q9;
            Q9=makeQuery(id+"F0.imprint","IMPRINT",FACE,{"disambiguationData":[TD([[makeQuery(id+"F0.imprint","IMPRINT",EDGE,{"derivedFrom":sQuery(id+"F0.wireOp",EDGE,"E66.MirrorCS")}),1.0]])]});
            var Q10;
            Q10=makeQuery(id+"F0.imprint","IMPRINT",FACE,{"disambiguationData":[TD([[makeQuery(id+"F0.imprint","IMPRINT",EDGE,{"derivedFrom":sQuery(id+"F0.wireOp",EDGE,"E120")}),1.0]])]});
            var Q11;
            Q11=makeQuery(id+"F0.imprint","IMPRINT",FACE,{"disambiguationData":[TD([[makeQuery(id+"F0.imprint","IMPRINT",EDGE,{"derivedFrom":sQuery(id+"F0.wireOp",EDGE,"E130")}),-1.0]])]});
            var Q12;
            Q12=makeQuery(id+"F0.imprint","IMPRINT",FACE,{"disambiguationData":[TD([[makeQuery(id+"F0.imprint","IMPRINT",EDGE,{"derivedFrom":sQuery(id+"F0.wireOp",EDGE,"E168")}),-1.0]])]});
            var Q13;
            Q13=makeQuery(id+"F0.imprint","IMPRINT",FACE,{"disambiguationData":[TD([[makeQuery(id+"F0.imprint","IMPRINT",EDGE,{"derivedFrom":sQuery(id+"F0.wireOp",EDGE,"E2.rect.left")}),1.0]])]});
            var Q14;
            Q14=makeQuery(id+"F0.imprint","IMPRINT",FACE,{"disambiguationData":[TD([[makeQuery(id+"F0.imprint","IMPRINT",EDGE,{"derivedFrom":sQuery(id+"F0.wireOp",EDGE,"E2.rect.right")}),-1.0]])]});
            var Q15;
            Q15=makeQuery(id+"F0.imprint","IMPRINT",FACE,{"disambiguationData":[TD([[makeQuery(id+"F0.imprint","IMPRINT",EDGE,{"derivedFrom":sQuery(id+"F0.wireOp",EDGE,"E2.rect.top")}),1.0]])]});
            var Q16;
            {var subQ1=sQuery(id+"F0.wireOp",EDGE,"E111");Q16=makeQuery(id+"F0.imprint","IMPRINT",FACE,{"disambiguationData":[TD([[makeQuery(id+"F0.imprint","IMPRINT",EDGE,{"derivedFrom":subQ1}),-1.0]])]});}
            var Q17;
            {var subQ2=sQuery(id+"F0.wireOp",EDGE,"E114");Q17=makeQuery(id+"F0.imprint","IMPRINT",FACE,{"disambiguationData":[TD([[makeQuery(id+"F0.imprint","IMPRINT",EDGE,{"derivedFrom":subQ2}),1.0]])]});}
            var Q18;
            Q18=makeQuery(id+"F0.imprint","IMPRINT",FACE,{"disambiguationData":[TD([[makeQuery(id+"F0.imprint","IMPRINT",EDGE,{"derivedFrom":sQuery(id+"F0.wireOp",EDGE,"E117")}),-1.0]])]});
            var Q19;
            Q19=makeQuery(id+"F0.imprint","IMPRINT",FACE,{"disambiguationData":[TD([[makeQuery(id+"F0.imprint","IMPRINT",EDGE,{"derivedFrom":sQuery(id+"F0.wireOp",EDGE,"E127")}),1.0]])]});
            var Q20;
            Q20=makeQuery(id+"F0.imprint","IMPRINT",FACE,{"disambiguationData":[TD([[makeQuery(id+"F0.imprint","IMPRINT",EDGE,{"derivedFrom":sQuery(id+"F0.wireOp",EDGE,"E139")}),1.0]])]});
            var Q21;
            Q21=makeQuery(id+"F0.imprint","IMPRINT",FACE,{"disambiguationData":[TD([[makeQuery(id+"F0.imprint","IMPRINT",EDGE,{"derivedFrom":sQuery(id+"F0.wireOp",EDGE,"E21.MirrorCS")}),1.0]])]});
            var Q22;
            Q22=makeQuery(id+"F0.imprint","IMPRINT",FACE,{"disambiguationData":[TD([[makeQuery(id+"F0.imprint","IMPRINT",EDGE,{"derivedFrom":sQuery(id+"F0.wireOp",EDGE,"E6")}),-1.0]])]});
            var Q23;
            {var subQ1=sQuery(id+"F0.wireOp",EDGE,"E47");Q23=makeQuery(id+"F0.imprint","IMPRINT",FACE,{"disambiguationData":[TD([[makeQuery(id+"F0.imprint","IMPRINT",EDGE,{"derivedFrom":subQ1}),-1.0]])]});}
            extrude(context, id + "F1", {"entities" : qUnion([Q0, Q1, Q2, Q3, Q4, Q5, Q6, Q7, Q8, Q9, Q10, Q11, Q12, Q13, Q14, Q15, Q16, Q17, Q18, Q19, Q20, Q21, Q22, Q23]), "depth" : 1.7 * mm});
        }
    });
